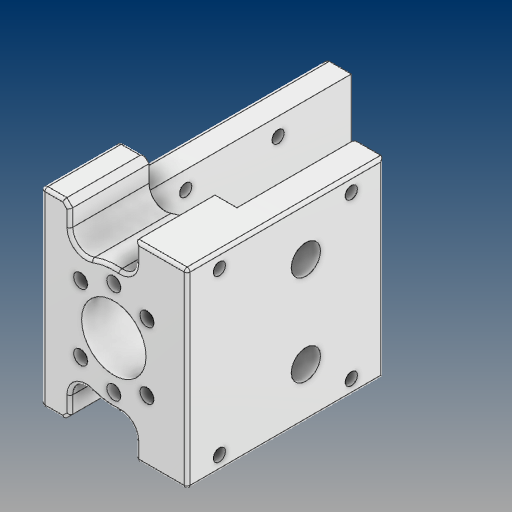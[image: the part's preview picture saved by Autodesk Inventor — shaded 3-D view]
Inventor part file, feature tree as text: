
AUTODESK INVENTOR PART (.ipt)
format: ipt  version: 2021 (Build 250183000, 183)  size: 436,736 bytes
history: native  units: mm
features: extrude x10, sketch x9, projected_geometry x9, reference x6, other x6, fillet x5, plane x1, mirror x1, chamfer x1
ambient origin geometry x8: Origin, YZ Plane, XZ Plane, XY Plane, X Axis, Y Axis, Z Axis, Center Point
bodies: Solid1 (feature_tree)
feature tree (48):
  sketch  "Sketch1"  dims[d0=30.0mm d1=21.0mm]
  plane  "Work Plane1"
  extrude  "Extrusion1"  Depth=21.0mm
  extrude  "Extrusion2"  Depth=30.0mm
  extrude  "Extrusion3"  Depth=15.0mm
  extrude  "Extrusion4"  Depth=10.0mm
  mirror  "Mirror1"
  extrude  "Extrusion5"  Depth=31.0mm
  fillet  "Fillet1"  Radius=5.0mm
  chamfer  "Chamfer1"  Distance=10.0mm
  fillet  "Fillet2"  Radius=10.0mm
  fillet  "Fillet3"  Radius=20.0mm
  sketch  "Sketch7"  dims[d18=4.2mm d19=10.0mm d20=0.0mm d21=10.0mm d22=0.0mm d23=20.0mm]
  extrude  "Extrusion6"  Depth=10.0mm TaperAngle=0.0deg
  extrude  "Extrusion7"  Depth=2.0mm TaperAngle=45.0deg
  extrude  "Extrusion8"  Depth=1.0mm
  fillet  "Fillet4"  Radius=40.0mm
  fillet  "Fillet5"  Radius=45.0mm
  extrude  "Extrusion9"  Depth=5.0mm
  extrude  "Extrusion10"  Depth=1.0mm
  reference  "Reference1"
  sketch  "Sketch3"  dims[d2=30.0mm d3=65.0mm]
  projected_geometry  "Projected Loop2"
  sketch  "Sketch4"  dims[d4=8.0mm d5=15.0mm]
  projected_geometry  "Projected Loop3"
  reference  "Reference2"
  reference  "Reference3"
  sketch  "Sketch5"  dims[d6=10.0mm d7=0.0mm d12=50.0mm]
  reference  "Reference4"
  reference  "Reference5"
  projected_geometry  "Projected Loop4"
  projected_geometry  "Projected Loop5"
  sketch  "Sketch6"  dims[d15=31.5mm d16=31.0mm d17=5.0mm]
  reference  "Reference6"
  projected_geometry  "Projected Loop6"
  projected_geometry  "Projected Loop7"
  sketch  "Sketch8"  dims[d24=10.0mm d25=0.0mm d26=34.5mm d27=0.0mm]
  projected_geometry  "Projected Loop8"
  projected_geometry  "Projected Loop9"
  sketch  "Sketch9"  dims[d28=5.5mm d29=2.0mm d30=2.0mm d31=45.0deg]
  sketch  "Sketch10"  dims[d32=1.5mm d33=5.25mm d34=40.0mm d35=45.0mm d36=5.0mm d37=4.2mm d38=10.0mm d39=0.0mm d40=13.25mm d41=0.0mm d42=30.0mm d43=10.0mm d44=15.75mm d45=0.0mm d46=1.0mm d47=1.0mm d48=21.25mm d49=0.0mm d50=32.0mm d51=1.0mm d52=0.0mm d53=0.0mm]
  projected_geometry  "Projected Loop10"
  other  "<userpath>\Desktop\DO_AN_TOT_NGHIEP_2024\Mechanical\Design_in_3D\Version_1\0012_Bo_truot.iam"
  other  "0012_Bo_truot.iam"
  other  "1204 BALL NUT:1"
  other  "HGR20.ipt:1"
  other  "HGR20C:1"
  other  "HGR20C:3"
